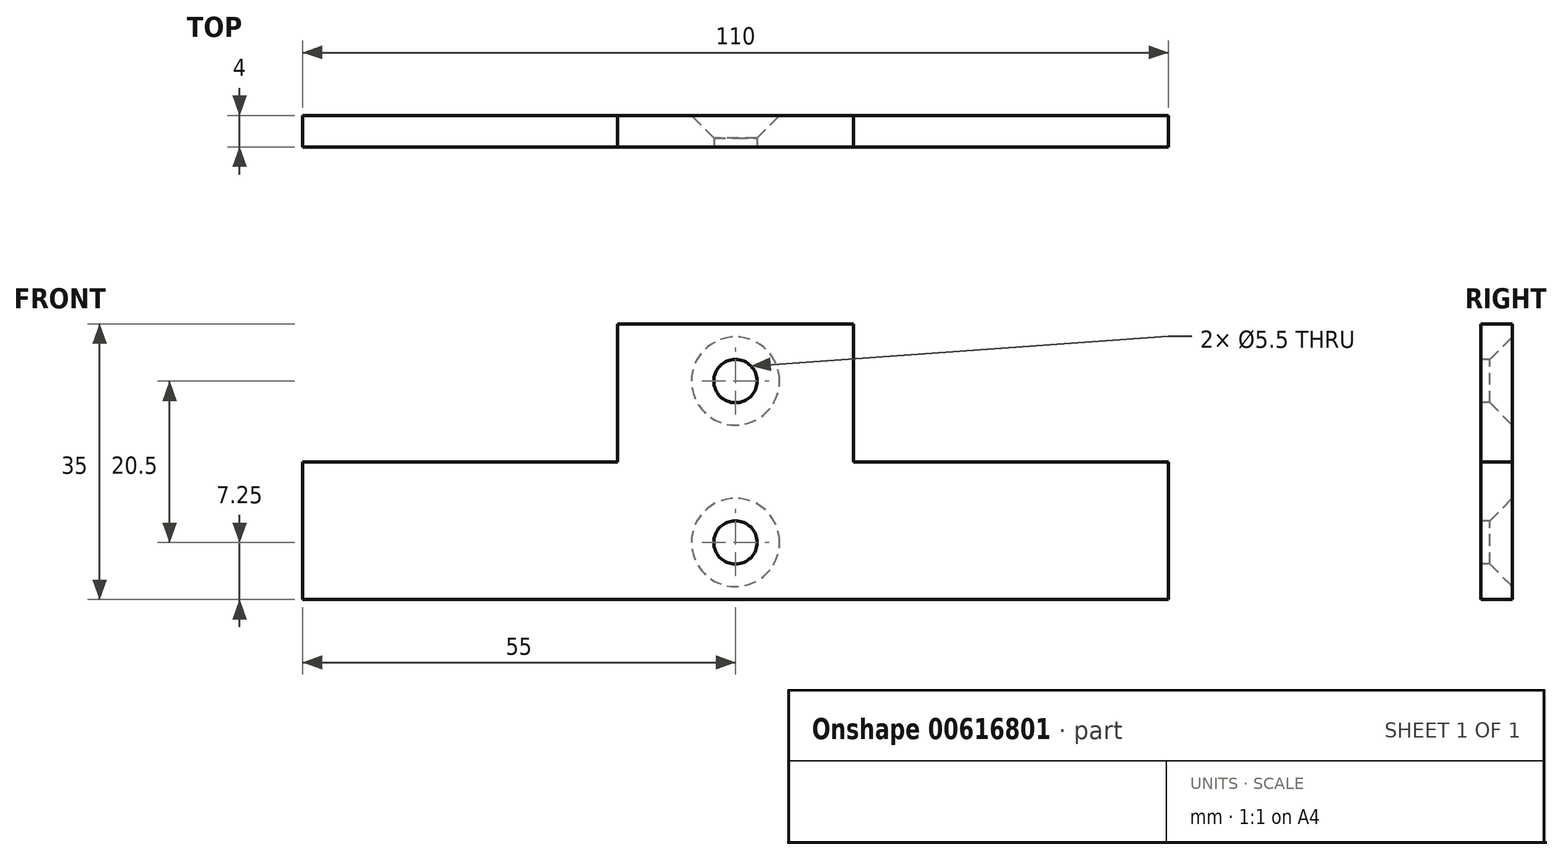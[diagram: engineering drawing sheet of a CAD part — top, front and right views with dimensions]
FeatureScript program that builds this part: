
annotation { "Feature Type Name" : "Feature", "Feature Type Description" : "" }
export const myFeature = defineFeature(function(context is Context, id is Id, definition is map)
    precondition{}
    {
        {
            var Q0;
            Q0=qCreatedBy(makeId("Front.planeOp"),FACE);
            var sketch = newSketch(context, id + "F0", { "sketchPlane" : qUnion([Q0])});
            skPoint(sketch, "E0", {"position": v(0, 10.25) * mm});
            skPoint(sketch, "E1", {"position": v(0, -10.25) * mm});
            skLineSegment(sketch, "E2.bottom", {"start": v(15, 17.5) * mm, "end": v(-15, 17.5) * mm});
            skLineSegment(sketch, "E2.top", {"start": v(55, -17.5) * mm, "end": v(-55, -17.5) * mm});
            skLineSegment(sketch, "E2.left", {"start": v(55, 0) * mm, "end": v(55, -17.5) * mm});
            skLineSegment(sketch, "E2.right", {"start": v(-55, 0) * mm, "end": v(-55, -17.5) * mm});
            skPoint(sketch, "E2.middle", {"position": v(0, 0) * mm});
            skLineSegment(sketch, "E3", {"start": v(-15, 17.5) * mm, "end": v(-15, 0) * mm});
            skLineSegment(sketch, "E4", {"start": v(-15, 0) * mm, "end": v(-55, 0) * mm});
            skLineSegment(sketch, "E5.MirrorCS", {"start": v(15, 17.5) * mm, "end": v(15, 0) * mm});
            skLineSegment(sketch, "E6.MirrorCS", {"start": v(15, 0) * mm, "end": v(55, 0) * mm});
            skSolve(sketch);
        }
        {
            var Q0;
            Q0=makeQuery(id+"F0.imprint","IMPRINT",FACE,{"disambiguationData":[TD([[makeQuery(id+"F0.imprint","IMPRINT",EDGE,{"derivedFrom":sQuery(id+"F0.wireOp",EDGE,"E2.bottom")}),1.0]])]});
            extrude(context, id + "F1", {"entities" : qUnion([Q0]), "depth" : 4 * mm, "offsetDistance" : 25 * mm});
        }
        {
            var Q0;
            Q0=sQuery(id+"F0.wireOp",VERTEX,"E0");
            var Q1;
            Q1=sQuery(id+"F0.wireOp",VERTEX,"E1");
            var Q2;
            Q2=makeQuery(id+"F1.opExtrude","SWEPT_BODY",BODY,{"disambiguationData":[OSD([sQuery(id+"F0.wireOp",EDGE,"E2.bottom"),sQuery(id+"F0.wireOp",EDGE,"E2.top"),sQuery(id+"F0.wireOp",EDGE,"E2.left"),sQuery(id+"F0.wireOp",EDGE,"E2.right"),sQuery(id+"F0.wireOp",EDGE,"E3"),sQuery(id+"F0.wireOp",EDGE,"E4"),sQuery(id+"F0.wireOp",EDGE,"E5.MirrorCS"),sQuery(id+"F0.wireOp",EDGE,"E6.MirrorCS")])]});
            hole(context, id + "F2", {"style" : HoleStyle.C_SINK, "endStyle" : HoleEndStyle.THROUGH, "oppositeDirection" : true, "standardTappedOrClearance" : lookupTablePath({ "fit" : "Normal", "standard" : "ISO", "size" : "M5", "type" : "Clearance" }), "standardBlindInLast" : lookupTablePath({ "fit" : "Standard", "standard" : "ISO", "size" : "M5", "type" : "Clearance" }), "holeDiameter" : 5.5 * mm, "cSinkDiameter" : 11.2 * mm, "cSinkAngle" : 90 * degree, "majorDiameter" : 5 * mm, "isTappedThrough" : true, "tappedDepth" : 3.9 * mm, "tapClearance" : 3, "locations" : qUnion([Q0, Q1]), "scope" : qUnion([Q2]), "startStyle" : HoleStartStyle.PART});
        }
    });
